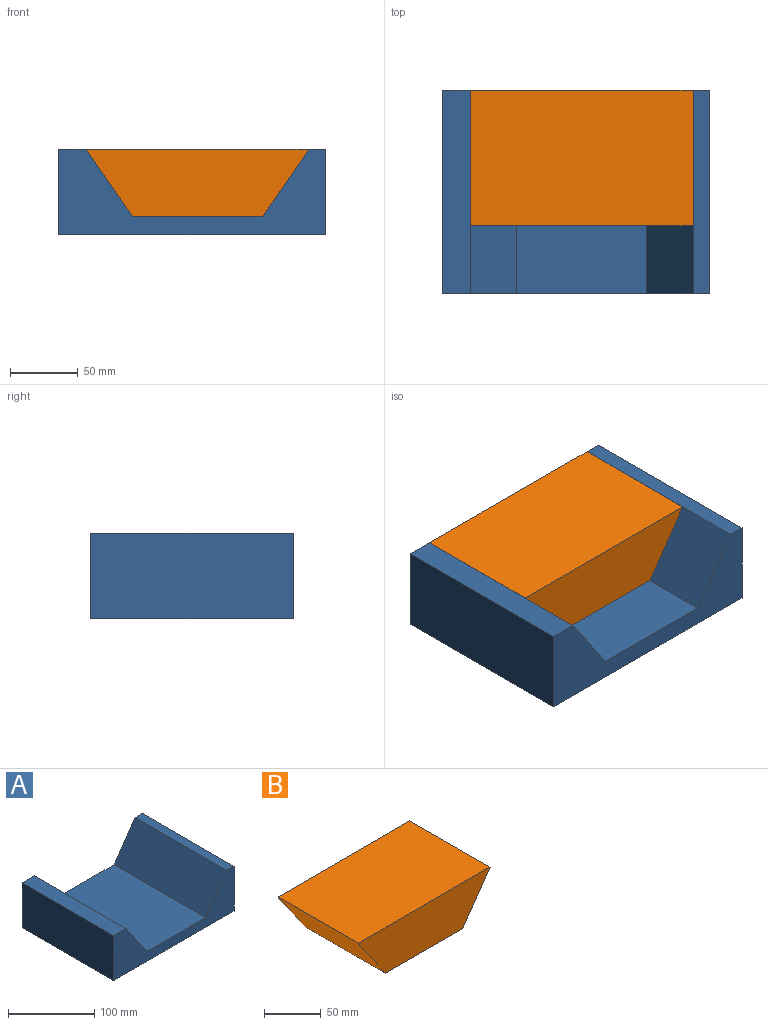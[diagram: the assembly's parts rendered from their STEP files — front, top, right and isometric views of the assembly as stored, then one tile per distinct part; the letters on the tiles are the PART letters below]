
ASSEMBLY  parts=2 mates=1
PART A: 10 faces, bbox 197.1x150x63.5 mm
  f0: plane 150x49.55mm, normal (0.82,0,0.57), area 9036.5mm2, adj f1,f7,f8,f9
  f1: plane 150x20.29mm, normal (0,0,1), area 3044.1mm2, adj f0,f2,f8,f9
  f2: plane 150x63.54mm, normal (-1,0,0), area 9531.6mm2, adj f1,f3,f8,f9
  f3: plane 197.08x150mm, normal (0,0,-1), area 29562.6mm2, adj f2,f4,f8,f9
  f4: plane 150x63.54mm, normal (1,0,0), area 9531.6mm2, adj f3,f5,f8,f9
  f5: plane 150x12.01mm, normal (0,0,1), area 1802.2mm2, adj f4,f6,f8,f9
  f6: plane 150x49.55mm, normal (-0.82,0,0.57), area 9036.5mm2, adj f5,f7,f8,f9
  f7: plane 150x96.24mm, normal (0,0,1), area 14435.7mm2, adj f0,f6,f8,f9
  f8: plane 197.08x63.54mm, normal (0,-1,0), area 6057.3mm2, adj f0,f1,f2,f3,f4,f5,f6,f7
  f9: plane 197.08x63.54mm, normal (0,1,0), area 6057.3mm2, adj f0,f1,f2,f3,f4,f5,f6,f7
PART B: 6 faces, bbox 164.8x100x49.5 mm
  f0: plane 164.78x100mm, normal (0,0,1), area 16477.5mm2, adj f1,f3,f4,f5
  f1: plane 100x49.55mm, normal (-0.82,0,-0.57), area 6024.3mm2, adj f0,f2,f4,f5
  f2: plane 100x96.24mm, normal (0,0,-1), area 9623.8mm2, adj f1,f3,f4,f5
  f3: plane 100x49.55mm, normal (0.82,0,-0.57), area 6024.3mm2, adj f0,f2,f4,f5
  f4: plane 164.78x49.55mm, normal (0,-1,0), area 6466.2mm2, adj f0,f1,f2,f3
  f5: plane 164.78x49.55mm, normal (0,1,0), area 6466.2mm2, adj f0,f1,f2,f3
PLACE A t=(121.99,-270.7,27.21)mm
PLACE B t=(121.99,-270.7,27.21)mm
MATE slider A.f9 <-> B.f5  axis (0,1,0) through (170.11,-270.7,27.21)mm
